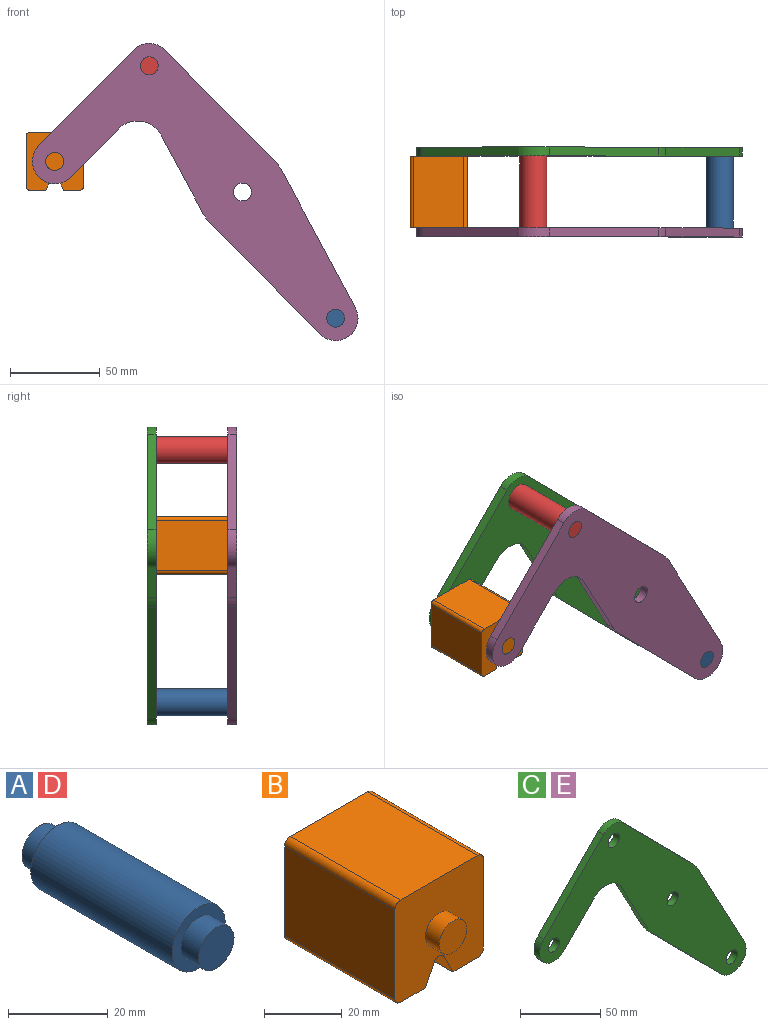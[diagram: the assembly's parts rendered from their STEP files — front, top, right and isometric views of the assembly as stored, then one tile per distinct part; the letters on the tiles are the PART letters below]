
ASSEMBLY  parts=5 mates=3
PART A: 7 faces, bbox 15x50x15 mm
  f0: cylinder r=7.5mm len=40mm, axis (0,-1,0), area 1885mm2, adj f2,f5
  f1: cylinder r=5mm len=10mm, axis (0,1,0), area 157.1mm2, adj f2,f3
  f2: plane 15x15mm, normal (0,-1,0), area 98.2mm2, adj f0,f1
  f3: plane 10x10mm, normal (0,-1,0), area 78.5mm2, adj f1
  f4: cylinder r=5mm len=10mm, axis (0,-1,0), area 157.1mm2, adj f5,f6
  f5: plane 15x15mm, normal (0,1,0), area 98.2mm2, adj f0,f4
  f6: plane 10x10mm, normal (0,1,0), area 78.5mm2, adj f4
PART B: 18 faces, bbox 32.1x50x32.1 mm
  f0: plane 40x28.08mm, normal (1,0,0), area 1123.1mm2, adj f4,f10,f13,f14
  f1: plane 40x9.04mm, normal (0,0,-1), area 361.6mm2, adj f2,f4,f10,f14
  f2: plane 40x6.42mm, normal (-0.89,0,-0.45), area 287.2mm2, adj f1,f4,f10,f15
  f3: plane 40x6.42mm, normal (0.89,0,-0.45), area 287.2mm2, adj f4,f5,f10,f15
  f4: plane 32.08x32.08mm, normal (0,-1,0), area 900.6mm2, adj f0,f1,f2,f3,f5,f6,f7,f9
  f5: plane 40x9.04mm, normal (0,0,-1), area 361.6mm2, adj f3,f4,f10,f16
  f6: plane 40x28.08mm, normal (0,0,1), area 1123.1mm2, adj f4,f10,f13,f17
  f7: plane 40x28.08mm, normal (-1,0,0), area 1123.1mm2, adj f4,f10,f16,f17
  f8: plane 10x10mm, normal (0,-1,0), area 78.5mm2, adj f9
  f9: cylinder r=5mm len=10mm, axis (0,1,0), area 157.1mm2, adj f4,f8
  f10: plane 32.08x32.08mm, normal (0,1,0), area 900.6mm2, adj f0,f1,f2,f3,f5,f6,f7,f12
  f11: plane 10x10mm, normal (0,1,0), area 78.5mm2, adj f12
  f12: cylinder r=5mm len=10mm, axis (0,-1,0), area 157.1mm2, adj f10,f11
  f13: cylinder r=2mm len=40mm, axis (0,1,0), area 125.7mm2, adj f0,f4,f6,f10
  f14: cylinder r=2mm len=40mm, axis (0,-1,0), area 125.7mm2, adj f0,f1,f4,f10
  f15: cylinder r=2mm len=40mm, axis (0,1,0), area 177.1mm2, adj f2,f3,f4,f10
  f16: cylinder r=2mm len=40mm, axis (0,1,0), area 125.7mm2, adj f4,f5,f7,f10
  f17: cylinder r=2mm len=40mm, axis (0,-1,0), area 125.7mm2, adj f4,f6,f7,f10
PART C: 18 faces, bbox 181.7x5x165.8 mm
  f0: plane 43.49x23.35mm, normal (-0.88,0,-0.47), area 246.8mm2, adj f1,f14,f16,f17
  f1: cylinder r=25mm len=5.75mm, axis (0,1,0), area 35.8mm2, adj f0,f2,f16,f17
  f2: plane 61.6x60.87mm, normal (-0.71,0,-0.7), area 433mm2, adj f1,f3,f16,f17
  f3: cylinder r=12.5mm len=21.39mm, axis (0,1,0), area 178.4mm2, adj f2,f4,f16,f17
  f4: plane 76.3x40.96mm, normal (0.88,0,0.47), area 433mm2, adj f3,f5,f16,f17
  f5: cylinder r=25mm len=5.75mm, axis (0,1,0), area 35.8mm2, adj f4,f6,f16,f17
  f6: plane 61.6x60.87mm, normal (0.71,0,0.7), area 433mm2, adj f5,f7,f16,f17
  f7: cylinder r=12.5mm len=17.78mm, axis (0,1,0), area 98.9mm2, adj f6,f8,f16,f17
  f8: plane 53.35x52.71mm, normal (-0.71,0,0.7), area 375mm2, adj f7,f9,f16,f17
  f9: cylinder r=12.5mm len=21.39mm, axis (0,1,0), area 196.3mm2, adj f8,f10,f16,f17
  f10: plane 26.86x26.54mm, normal (0.71,0,-0.7), area 188.8mm2, adj f9,f14,f16,f17
  f11: cylinder r=5mm len=10mm, axis (0,1,0), area 157.1mm2, adj f16,f17
  f12: cylinder r=5mm len=10mm, axis (0,1,0), area 157.1mm2, adj f16,f17
  f13: cylinder r=5mm len=10mm, axis (0,1,0), area 157.1mm2, adj f16,f17
  f14: cylinder r=15mm len=23.89mm, axis (0,1,0), area 140.2mm2, adj f0,f10,f16,f17
  f15: cylinder r=5mm len=10mm, axis (0,1,0), area 157.1mm2, adj f16,f17
  f16: plane 181.66x165.78mm, normal (0,-1,0), area 8710.1mm2, adj f0,f1,f2,f3,f4,f5,f6,f7
  f17: plane 181.66x165.78mm, normal (0,1,0), area 8710.1mm2, adj f0,f1,f2,f3,f4,f5,f6,f7
PART D: same geometry as A
PART E: same geometry as C
PLACE A t=(103.95,-20,-140.78)mm
PLACE B t=(0,-20,0)mm
PLACE C t=(0,25,0)mm
PLACE D t=(0,-20,0)mm
PLACE E t=(0,-20,0)mm fixed
MATE fastened A.f0 <-> E.f3  axis (0,-1,0) through (51.98,-20,-70.39)mm
MATE revolute B.f9 <-> E.f9  axis (0,-1,0) through (-104.69,-20,17.04)mm
MATE fastened C.f7 <-> D.f0  axis (0,-1,0) through (-51.98,20,70.39)mm
